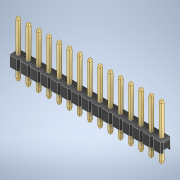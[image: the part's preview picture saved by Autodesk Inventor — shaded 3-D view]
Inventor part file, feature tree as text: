
AUTODESK INVENTOR PART (.ipt)
format: ipt  version: 2021 (Build 250183000, 183)  size: 472,064 bytes
history: native  units: in
note: dims shown in document units (in); Inventor stores cm internally (conversion verified against a paired STEP export)
features: other x14, chamfer x1, boolean_combine x1
ambient origin geometry x8: Origin, YZ Plane, XZ Plane, XY Plane, X Axis, Y Axis, Z Axis, Center Point
bodies: Solid1 (feature_tree), Solid2 (feature_tree), Solid3 (feature_tree), Solid4 (feature_tree), Solid5 (feature_tree), Solid6 (feature_tree), Solid7 (feature_tree), Solid8 (feature_tree), Solid9 (feature_tree), Solid10 (feature_tree), Solid11 (feature_tree), Solid12 (feature_tree), Solid13 (feature_tree), Solid14 (feature_tree), Solid15 (feature_tree), Solid16 (feature_tree)
feature tree (16):
  chamfer  "Chamfer3"  [1 undecoded]
  other  "LPattern1[1]"
  other  "LPattern1[2]"
  other  "LPattern1[3]"
  other  "LPattern1[4]"
  other  "LPattern1[5]"
  other  "LPattern1[6]"
  other  "LPattern1[7]"
  other  "LPattern1[8]"
  other  "LPattern1[9]"
  other  "LPattern1[10]"
  other  "LPattern1[11]"
  other  "LPattern1[12]"
  other  "LPattern1[13]"
  other  "LPattern1[14]"
  boolean_combine  "Combine1"
note: 1 required parameter value undecoded (feature->parameter linkage not recoverable at this tier; creation-order binding heuristic only, values carry confidence <= 0.55)
